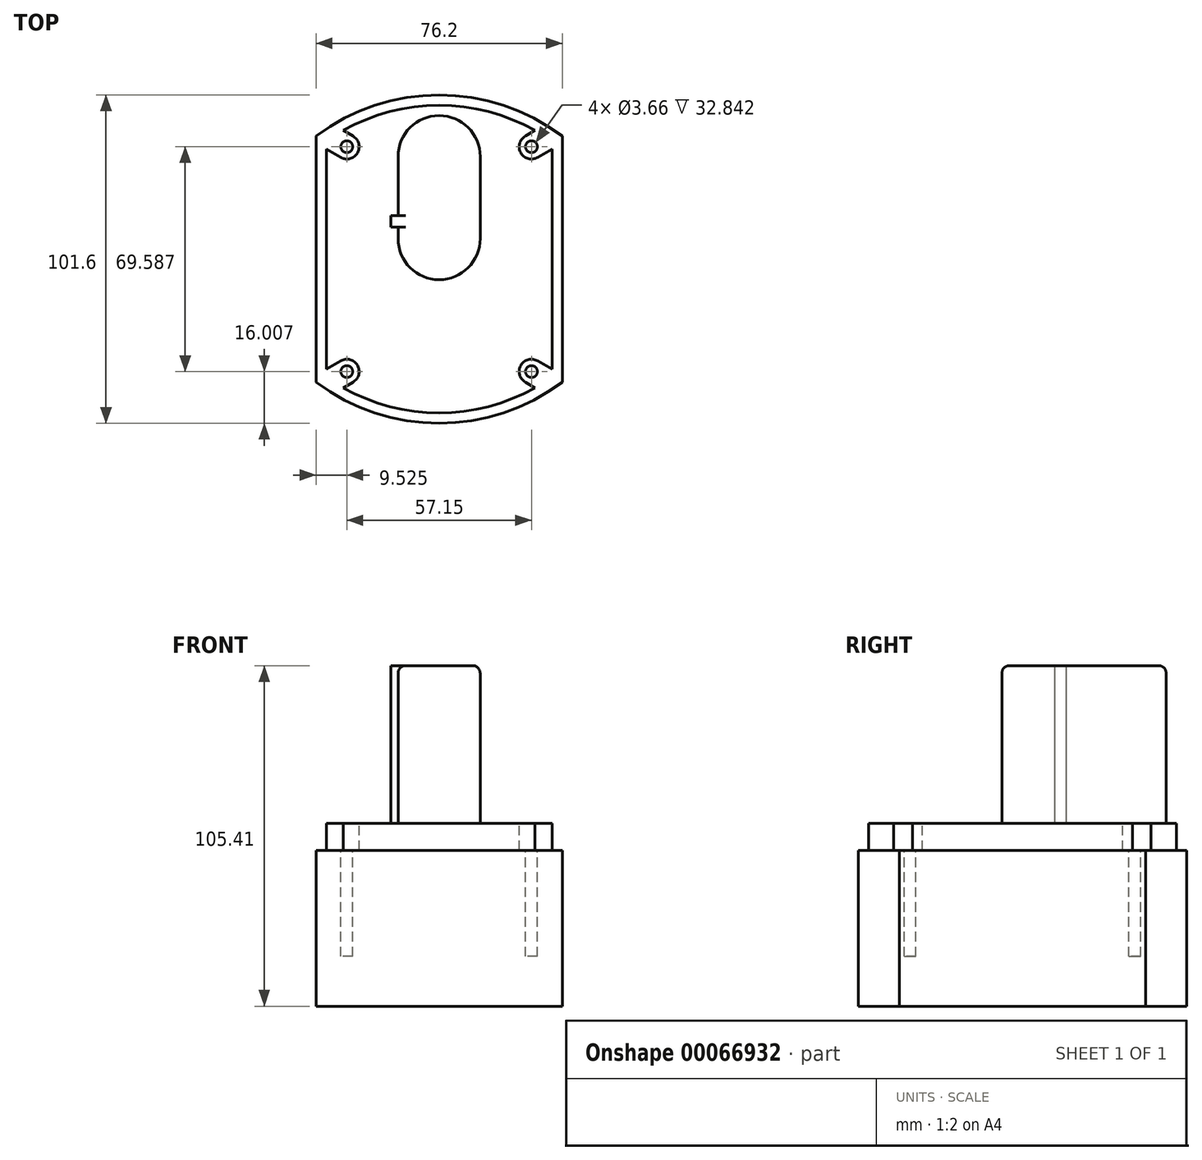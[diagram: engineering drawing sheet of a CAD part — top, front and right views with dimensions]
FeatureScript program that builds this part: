
annotation { "Feature Type Name" : "Feature", "Feature Type Description" : "" }
export const myFeature = defineFeature(function(context is Context, id is Id, definition is map)
    precondition{}
    {
        {
            var Q0;
            Q0=qCreatedBy(makeId("Top.planeOp"),FACE);
            var sketch = newSketch(context, id + "F0", { "sketchPlane" : qUnion([Q0])});
            skLineSegment(sketch, "E0.rect.bottom", {"start": v(38.1, -38.1) * mm, "end": v(-38.1, -38.1) * mm, "construction": true});
            skLineSegment(sketch, "E0.rect.top", {"start": v(38.1, 38.1) * mm, "end": v(-38.1, 38.1) * mm, "construction": true});
            skLineSegment(sketch, "E0.rect.left", {"start": v(38.1, -38.1) * mm, "end": v(38.1, 38.1) * mm});
            skLineSegment(sketch, "E0.rect.right", {"start": v(-38.1, -38.1) * mm, "end": v(-38.1, 38.1) * mm});
            skPoint(sketch, "E0.rect.middle", {"position": v(0, 0) * mm});
            skLineSegment(sketch, "E1", {"start": v(0, 38.1) * mm, "end": v(0, 50.8) * mm, "construction": true});
            skArc(sketch, "E2", {"start": v(38.1, 38.1) * mm, "mid": v(0, 50.8) * mm, "end": v(-38.1, 38.1) * mm});
            skLineSegment(sketch, "E3", {"start": v(-38.1, 0) * mm, "end": v(38.1, 0) * mm, "construction": true});
            skArc(sketch, "E4.MirrorCS", {"start": v(38.1, -38.1) * mm, "mid": v(0, -50.8) * mm, "end": v(-38.1, -38.1) * mm});
            skSolve(sketch);
        }
        {
            var Q0;
            Q0=makeQuery(id+"F0.imprint","IMPRINT",FACE,{"disambiguationData":[TD([[makeQuery(id+"F0.imprint","IMPRINT",EDGE,{"derivedFrom":sQuery(id+"F0.wireOp",EDGE,"E0.rect.left")}),1.0]])]});
            extrude(context, id + "F1", {"entities" : qUnion([Q0]), "oppositeDirection" : true, "depth" : 48.26 * mm});
        }
        {
            var Q0;
            Q0=makeQuery(id+"F1.opExtrude","CAP_FACE",FACE,{"disambiguationData":[OSD([sQuery(id+"F0.wireOp",EDGE,"E0.rect.left"),sQuery(id+"F0.wireOp",EDGE,"E0.rect.right"),sQuery(id+"F0.wireOp",EDGE,"E2"),sQuery(id+"F0.wireOp",EDGE,"E4.MirrorCS")])],"isStart":true});
            var sketch = newSketch(context, id + "F2", { "sketchPlane" : qUnion([Q0])});
            skArc(sketch, "E5.0.0", {"start": v(-38.1, -38.1) * mm, "mid": v(0, -50.8) * mm, "end": v(38.1, -38.1) * mm, "construction": true});
            skLineSegment(sketch, "E5.0.1", {"start": v(38.1, -38.1) * mm, "end": v(38.1, 38.1) * mm, "construction": true});
            skArc(sketch, "E5.0.2", {"start": v(38.1, 38.1) * mm, "mid": v(0, 50.8) * mm, "end": v(-38.1, 38.1) * mm, "construction": true});
            skLineSegment(sketch, "E5.0.3", {"start": v(-38.1, 38.1) * mm, "end": v(-38.1, -38.1) * mm, "construction": true});
            skArc(sketch, "E6.0", {"start": v(-34.92, -36.49) * mm, "mid": v(0, -47.63) * mm, "end": v(34.92, -36.49) * mm});
            skLineSegment(sketch, "E6.1", {"start": v(-34.93, 36.49) * mm, "end": v(-34.92, -36.49) * mm});
            skArc(sketch, "E6.2", {"start": v(34.92, 36.49) * mm, "mid": v(0, 47.63) * mm, "end": v(-34.93, 36.49) * mm});
            skLineSegment(sketch, "E6.3", {"start": v(34.93, -36.49) * mm, "end": v(34.92, 36.49) * mm});
            skSolve(sketch);
        }
        {
            var Q0;
            Q0 = qSketchRegion(id + "F2", true);
            extrude(context, id + "F3", {"entities" : qUnion([Q0]), "operationType" : NewBodyOperationType.ADD, "depth" : 8.38 * mm});
        }
        {
            var Q0;
            Q0=makeQuery(id+"F3.opExtrude","CAP_FACE",FACE,{"disambiguationData":[OSD([sQuery(id+"F2.wireOp",EDGE,"E6.0"),sQuery(id+"F2.wireOp",EDGE,"E6.1"),sQuery(id+"F2.wireOp",EDGE,"E6.2"),sQuery(id+"F2.wireOp",EDGE,"E6.3")])],"isStart":false});
            var sketch = newSketch(context, id + "F4", { "sketchPlane" : qUnion([Q0])});
            skLineSegment(sketch, "E7.rect.bottom", {"start": v(28.57, 34.8) * mm, "end": v(-28.58, 34.8) * mm, "construction": true});
            skLineSegment(sketch, "E7.rect.top", {"start": v(28.58, -34.8) * mm, "end": v(-28.57, -34.8) * mm, "construction": true});
            skLineSegment(sketch, "E7.rect.left", {"start": v(28.57, 34.8) * mm, "end": v(28.58, -34.8) * mm, "construction": true});
            skLineSegment(sketch, "E7.rect.right", {"start": v(-28.58, 34.8) * mm, "end": v(-28.57, -34.8) * mm, "construction": true});
            skPoint(sketch, "E7.rect.middle", {"position": v(0, 0) * mm});
            skLineSegment(sketch, "E8", {"start": v(-28.58, -34.8) * mm, "end": v(-50.57, -47.5) * mm, "construction": true});
            skArc(sketch, "E9.0.startCap", {"start": v(-30.48, -31.5) * mm, "mid": v(-25.28, -32.89) * mm, "end": v(-26.67, -38.1) * mm});
            skArc(sketch, "E9.0.endCap", {"start": v(-48.67, -50.8) * mm, "mid": v(-53.87, -49.4) * mm, "end": v(-52.48, -44.2) * mm});
            skLineSegment(sketch, "E9.0.left", {"start": v(-26.67, -38.1) * mm, "end": v(-48.67, -50.8) * mm});
            skLineSegment(sketch, "E9.0.right", {"start": v(-30.48, -31.5) * mm, "end": v(-52.48, -44.2) * mm});
            skLineSegment(sketch, "E10", {"start": v(-28.57, 0) * mm, "end": v(28.57, 0) * mm, "construction": true});
            skLineSegment(sketch, "E11", {"start": v(0, 34.8) * mm, "end": v(0, -34.8) * mm, "construction": true});
            skLineSegment(sketch, "E12.MirrorCS", {"start": v(26.67, -38.1) * mm, "end": v(48.67, -50.8) * mm});
            skLineSegment(sketch, "E13.MirrorCS", {"start": v(30.48, -31.5) * mm, "end": v(52.48, -44.2) * mm});
            skArc(sketch, "E14.MirrorCS", {"start": v(48.67, -50.8) * mm, "mid": v(53.87, -49.4) * mm, "end": v(52.48, -44.2) * mm});
            skArc(sketch, "E15.MirrorCS", {"start": v(30.48, -31.5) * mm, "mid": v(25.28, -32.89) * mm, "end": v(26.67, -38.1) * mm});
            skLineSegment(sketch, "E16.MirrorCS", {"start": v(-30.48, 31.5) * mm, "end": v(-52.48, 44.2) * mm});
            skLineSegment(sketch, "E17.MirrorCS", {"start": v(-26.67, 38.1) * mm, "end": v(-48.67, 50.8) * mm});
            skArc(sketch, "E18.MirrorCS", {"start": v(-48.67, 50.8) * mm, "mid": v(-53.87, 49.4) * mm, "end": v(-52.48, 44.2) * mm});
            skArc(sketch, "E19.MirrorCS", {"start": v(-30.48, 31.5) * mm, "mid": v(-25.28, 32.89) * mm, "end": v(-26.67, 38.1) * mm});
            skArc(sketch, "E20.MirrorCS", {"start": v(30.48, 31.5) * mm, "mid": v(25.28, 32.89) * mm, "end": v(26.67, 38.1) * mm});
            skLineSegment(sketch, "E21.MirrorCS", {"start": v(30.48, 31.5) * mm, "end": v(52.48, 44.2) * mm});
            skLineSegment(sketch, "E22.MirrorCS", {"start": v(26.67, 38.1) * mm, "end": v(48.67, 50.8) * mm});
            skArc(sketch, "E23.MirrorCS", {"start": v(48.67, 50.8) * mm, "mid": v(53.87, 49.4) * mm, "end": v(52.48, 44.2) * mm});
            skCircle(sketch, "E24", {"center": v(-28.58, 34.8) * mm, "radius": 1.83 * mm, "construction": true});
            skCircle(sketch, "E25", {"center": v(28.57, 34.8) * mm, "radius": 1.83 * mm, "construction": true});
            skCircle(sketch, "E26", {"center": v(28.58, -34.8) * mm, "radius": 1.83 * mm, "construction": true});
            skCircle(sketch, "E27", {"center": v(-28.57, -34.8) * mm, "radius": 1.83 * mm, "construction": true});
            skSolve(sketch);
        }
        {
            var Q0;
            Q0 = qSketchRegion(id + "F4", true);
            var Q1;
            Q1=makeQuery(id+"F1.opExtrude","CAP_FACE",FACE,{"disambiguationData":[OSD([sQuery(id+"F0.wireOp",EDGE,"E0.rect.left"),sQuery(id+"F0.wireOp",EDGE,"E0.rect.right"),sQuery(id+"F0.wireOp",EDGE,"E2"),sQuery(id+"F0.wireOp",EDGE,"E4.MirrorCS")])],"isStart":true});
            extrude(context, id + "F5", {"entities" : qUnion([Q0]), "operationType" : NewBodyOperationType.REMOVE, "endBound" : BoundingType.UP_TO_SURFACE, "oppositeDirection" : true, "endBoundEntityFace" : qUnion([Q1]), "depth" : 25.4 * mm});
        }
        {
            var Q0;
            Q0=makeQuery(id+"F5.boolean.opBoolean","MERGE",FACE,{"derivedFrom":[makeQuery(id+"F1.opExtrude","CAP_FACE",FACE,{"disambiguationData":[OSD([sQuery(id+"F0.wireOp",EDGE,"E0.rect.left"),sQuery(id+"F0.wireOp",EDGE,"E0.rect.right"),sQuery(id+"F0.wireOp",EDGE,"E2"),sQuery(id+"F0.wireOp",EDGE,"E4.MirrorCS")])],"isStart":true}),makeQuery(id+"F5.opExtrude","CAP_FACE",FACE,{"disambiguationData":[OSD([sQuery(id+"F4.wireOp",EDGE,"E9.0.startCap"),sQuery(id+"F4.wireOp",EDGE,"E9.0.endCap"),sQuery(id+"F4.wireOp",EDGE,"E9.0.left"),sQuery(id+"F4.wireOp",EDGE,"E9.0.right")])],"isStart":false}),makeQuery(id+"F5.opExtrude","CAP_FACE",FACE,{"disambiguationData":[OSD([sQuery(id+"F4.wireOp",EDGE,"E12.MirrorCS"),sQuery(id+"F4.wireOp",EDGE,"E13.MirrorCS"),sQuery(id+"F4.wireOp",EDGE,"E14.MirrorCS"),sQuery(id+"F4.wireOp",EDGE,"E15.MirrorCS")])],"isStart":false}),makeQuery(id+"F5.opExtrude","CAP_FACE",FACE,{"disambiguationData":[OSD([sQuery(id+"F4.wireOp",EDGE,"E16.MirrorCS"),sQuery(id+"F4.wireOp",EDGE,"E17.MirrorCS"),sQuery(id+"F4.wireOp",EDGE,"E18.MirrorCS"),sQuery(id+"F4.wireOp",EDGE,"E19.MirrorCS")])],"isStart":false}),makeQuery(id+"F5.opExtrude","CAP_FACE",FACE,{"disambiguationData":[OSD([sQuery(id+"F4.wireOp",EDGE,"E20.MirrorCS"),sQuery(id+"F4.wireOp",EDGE,"E21.MirrorCS"),sQuery(id+"F4.wireOp",EDGE,"E22.MirrorCS"),sQuery(id+"F4.wireOp",EDGE,"E23.MirrorCS")])],"isStart":false})]});
            var sketch = newSketch(context, id + "F6", { "sketchPlane" : qUnion([Q0])});
            skCircle(sketch, "E28.0", {"center": v(28.58, -34.8) * mm, "radius": 1.83 * mm});
            skCircle(sketch, "E28.1", {"center": v(-28.57, -34.8) * mm, "radius": 1.83 * mm});
            skCircle(sketch, "E28.2", {"center": v(-28.58, 34.8) * mm, "radius": 1.83 * mm});
            skCircle(sketch, "E28.3", {"center": v(28.57, 34.8) * mm, "radius": 1.83 * mm});
            skSolve(sketch);
        }
        {
            var Q0;
            Q0 = qSketchRegion(id + "F6", true);
            extrude(context, id + "F7", {"entities" : qUnion([Q0]), "operationType" : NewBodyOperationType.REMOVE, "oppositeDirection" : true, "depth" : 32.84 * mm});
        }
        {
            var Q0;
            Q0=qCreatedBy(makeId("Top.planeOp"),FACE);
            var sketch = newSketch(context, id + "F8", { "sketchPlane" : qUnion([Q0])});
            skLineSegment(sketch, "E29", {"start": v(0, 6.35) * mm, "end": v(0, 31.75) * mm, "construction": true});
            skArc(sketch, "E30.0.startCap", {"start": v(12.7, 6.35) * mm, "mid": v(0, -6.35) * mm, "end": v(-12.7, 6.35) * mm});
            skArc(sketch, "E30.0.endCap", {"start": v(-12.7, 31.75) * mm, "mid": v(0, 44.45) * mm, "end": v(12.7, 31.75) * mm});
            skLineSegment(sketch, "E30.0.left", {"start": v(-12.7, 6.35) * mm, "end": v(-12.7, 31.75) * mm});
            skLineSegment(sketch, "E30.0.right", {"start": v(12.7, 6.35) * mm, "end": v(12.7, 31.75) * mm});
            skPoint(sketch, "E31", {"position": v(0, 19.05) * mm});
            skPoint(sketch, "E32", {"position": v(0, 44.45) * mm});
            skPoint(sketch, "E33", {"position": v(0, -6.35) * mm});
            skSolve(sketch);
        }
        {
            var Q0;
            Q0 = qSketchRegion(id + "F8", true);
            extrude(context, id + "F9", {"entities" : qUnion([Q0]), "operationType" : NewBodyOperationType.ADD, "depth" : 57.15 * mm});
        }
        {
            var Q0;
            Q0=makeQuery(id+"F3.opExtrude","CAP_FACE",FACE,{"disambiguationData":[OSD([sQuery(id+"F2.wireOp",EDGE,"E6.0"),sQuery(id+"F2.wireOp",EDGE,"E6.1"),sQuery(id+"F2.wireOp",EDGE,"E6.2"),sQuery(id+"F2.wireOp",EDGE,"E6.3")])],"isStart":false});
            var sketch = newSketch(context, id + "F10", { "sketchPlane" : qUnion([Q0])});
            skLineSegment(sketch, "E34.bottom", {"start": v(-12.7, 9.9) * mm, "end": v(-14.99, 9.9) * mm});
            skLineSegment(sketch, "E34.top", {"start": v(-12.7, 13.46) * mm, "end": v(-14.99, 13.46) * mm});
            skLineSegment(sketch, "E34.left", {"start": v(-12.7, 9.9) * mm, "end": v(-12.7, 13.46) * mm});
            skLineSegment(sketch, "E34.right", {"start": v(-14.99, 9.9) * mm, "end": v(-14.99, 13.46) * mm});
            skSolve(sketch);
        }
        {
            var Q0;
            Q0 = qSketchRegion(id + "F10", true);
            var Q1;
            Q1=makeQuery(id+"F9.opExtrude","CAP_FACE",FACE,{"disambiguationData":[OSD([sQuery(id+"F8.wireOp",EDGE,"E30.0.startCap"),sQuery(id+"F8.wireOp",EDGE,"E30.0.endCap"),sQuery(id+"F8.wireOp",EDGE,"E30.0.left"),sQuery(id+"F8.wireOp",EDGE,"E30.0.right")])],"isStart":false});
            extrude(context, id + "F11", {"entities" : qUnion([Q0]), "operationType" : NewBodyOperationType.ADD, "endBound" : BoundingType.UP_TO_SURFACE, "endBoundEntityFace" : qUnion([Q1]), "depth" : 25.4 * mm});
        }
        {
            var Q0;
            Q0=makeQuery(id+"F9.opExtrude","CAP_EDGE",EDGE,{"disambiguationData":[OSD([sQuery(id+"F8.wireOp",EDGE,"E30.0.right")])],"isStart":false});
            fillet(context, id + "F12", {"entities" : qUnion([Q0]), "radius" : 2.3 * mm, "tangentPropagation" : true, "allowEdgeOverflow" : false});
        }
    });
